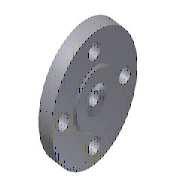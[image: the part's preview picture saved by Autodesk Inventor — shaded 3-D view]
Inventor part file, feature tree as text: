
AUTODESK INVENTOR PART (.ipt)
format: ipt  version: 2023.2 (Build 272271030, 271C)  size: 206,848 bytes
history: native  units: mm
features: sketch x2, revolve x1, extrude x1, pattern_circular x1
ambient origin geometry x8: Origin, YZ Plane, XZ Plane, XY Plane, X Axis, Y Axis, Z Axis, Center Point
bodies: Solid1 (feature_tree)
feature tree (5):
  revolve  "Revolution1"  [1 undecoded]
  extrude  "Extrusion1"  Depth=77.0mm
  pattern_circular  "Circular Pattern1"  Count=20  [1 undecoded]
  sketch  "Sketch1"  dims[d0=29.0mm d1=250.0mm]
  sketch  "Sketch2"  dims[d23=90.0deg d2=26.0mm d3=200.0mm d24=10.0mm d4=0.0mm d5=80.0mm d6=360.0deg d7=94.0mm d8=158.0mm d9=140.0mm d10=135.0deg d11=3.0mm d19=15.0mm d12=37.5mm d13=110.0mm d14=77.0mm d15=30.0deg d16=1.0mm d17=3.577925mm d18=124.0mm]
note: 2 required parameter values undecoded (feature->parameter linkage not recoverable at this tier; creation-order binding heuristic only, values carry confidence <= 0.55)